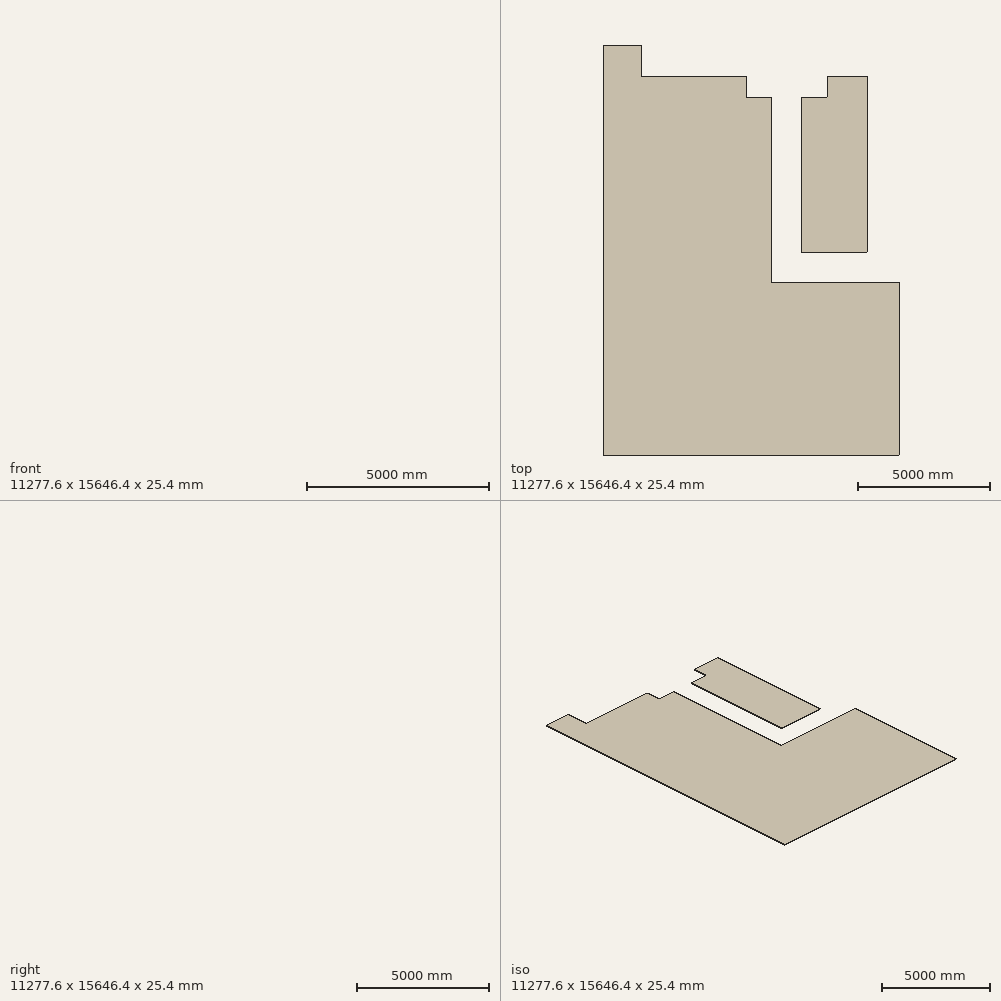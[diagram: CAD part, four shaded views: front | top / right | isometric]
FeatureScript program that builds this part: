
annotation { "Feature Type Name" : "Feature", "Feature Type Description" : "" }
export const myFeature = defineFeature(function(context is Context, id is Id, definition is map)
    precondition{}
    {
        {
            var Q0;
            Q0=qCreatedBy(makeId("Top.planeOp"),FACE);
            var sketch = newSketch(context, id + "F0", { "sketchPlane" : qUnion([Q0])});
            skLineSegment(sketch, "E0", {"start": v(0, 0) * mm, "end": v(939.8, 0) * mm});
            skLineSegment(sketch, "E1", {"start": v(939.8, 0) * mm, "end": v(939.8, -7061.2) * mm});
            skLineSegment(sketch, "E2", {"start": v(939.8, -7061.2) * mm, "end": v(4622.8, -7061.2) * mm});
            skLineSegment(sketch, "E3", {"start": v(5816.6, -13665.2) * mm, "end": v(-5461, -13665.2) * mm});
            skLineSegment(sketch, "E4", {"start": v(-5461, -13665.2) * mm, "end": v(-5461, 1981.2) * mm});
            skLineSegment(sketch, "E5", {"start": v(0, 787.4) * mm, "end": v(0, 0) * mm});
            skLineSegment(sketch, "E6", {"start": v(2082.8, 0) * mm, "end": v(2082.8, -5918.2) * mm});
            skLineSegment(sketch, "E7", {"start": v(2082.8, -5918.2) * mm, "end": v(4622.8, -5918.2) * mm});
            skLineSegment(sketch, "E8", {"start": v(2082.8, 0) * mm, "end": v(3073.4, 0) * mm});
            skLineSegment(sketch, "E9", {"start": v(3073.4, 0) * mm, "end": v(3073.4, 787.4) * mm});
            skLineSegment(sketch, "E10", {"start": v(4622.8, -5918.2) * mm, "end": v(4622.8, 787.4) * mm});
            skLineSegment(sketch, "E11", {"start": v(4622.8, 787.4) * mm, "end": v(3073.4, 787.4) * mm});
            skLineSegment(sketch, "E12", {"start": v(5816.6, -13665.2) * mm, "end": v(5816.6, -7061.2) * mm});
            skLineSegment(sketch, "E13", {"start": v(5816.6, -7061.2) * mm, "end": v(4622.8, -7061.2) * mm});
            skLineSegment(sketch, "E14", {"start": v(4622.8, -5918.2) * mm, "end": v(5816.6, -5918.2) * mm});
            skLineSegment(sketch, "E15", {"start": v(5816.6, -5918.2) * mm, "end": v(5816.6, 1422.4) * mm});
            skLineSegment(sketch, "E16", {"start": v(-5461, 1981.2) * mm, "end": v(-4013.2, 1981.2) * mm});
            skLineSegment(sketch, "E17", {"start": v(-4013.2, 1981.2) * mm, "end": v(-4013.2, 787.4) * mm});
            skLineSegment(sketch, "E18", {"start": v(-4013.2, 787.4) * mm, "end": v(0, 787.4) * mm});
            skLineSegment(sketch, "E19", {"start": v(5816.6, 1422.4) * mm, "end": v(-4013.2, 1422.4) * mm});
            skLineSegment(sketch, "E20", {"start": v(5816.6, -7061.2) * mm, "end": v(5816.6, -5918.2) * mm});
            skSolve(sketch);
        }
        {
            var Q0;
            Q0=makeQuery(id+"F0.imprint","IMPRINT",FACE,{"disambiguationData":[TD([[makeQuery(id+"F0.imprint","IMPRINT",EDGE,{"derivedFrom":sQuery(id+"F0.wireOp",EDGE,"E0")}),-1.0]])]});
            var Q1;
            Q1=makeQuery(id+"F0.imprint","IMPRINT",FACE,{"disambiguationData":[TD([[makeQuery(id+"F0.imprint","IMPRINT",EDGE,{"derivedFrom":sQuery(id+"F0.wireOp",EDGE,"E6")}),1.0]])]});
            extrude(context, id + "F1", {"entities" : qUnion([Q0, Q1]), "depth" : 25.4 * mm});
        }
    });
